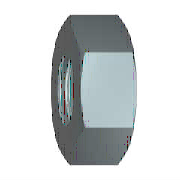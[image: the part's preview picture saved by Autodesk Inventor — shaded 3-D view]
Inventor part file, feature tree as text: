
AUTODESK INVENTOR PART (.ipt)
format: ipt  version: 2020 (Build 240168000, 168)  size: 165,376 bytes
history: native  units: mm (DEFAULTED — no unit token found)
features: sketch x3, chamfer x1, hole x1, other x1, plane x1
ambient origin geometry x7: Origin, YZ Plane, XZ Plane, X Axis, Y Axis, Z Axis, Center Point
bodies: Solid1 (feature_tree), Body (feature_tree)
feature tree (7):
  chamfer  "Chamfer1"  Angle=30.0deg  [1 undecoded]
  hole  "Thread"  [1 undecoded]
  other  "Work Axis1"
  plane  "Work Plane1"
  sketch  "Sketch1"  dims[d0=6.350853mm]
  sketch  "Sketch2"  dims[d1=2.4mm]
  sketch  "Sketch3"  dims[d2=0.0mm d3=30.0deg d4=30.0deg d5=4.6mm d6=4.6mm d7=90.0deg d25=2.459mm d26=6.0mm d27=4.0mm d28=2.0mm d29=14.3117mm d30=8.0mm d31=20.594885mm d8=0.270633mm d9=30.0deg d10=0.270633mm d11=30.0deg d13=0.0mm d14=0.0mm d39=0.0mm d40=0.270633mm d41=0.270633mm d42=0.0mm]
note: 2 required parameter values undecoded (feature->parameter linkage not recoverable at this tier; creation-order binding heuristic only, values carry confidence <= 0.55)
